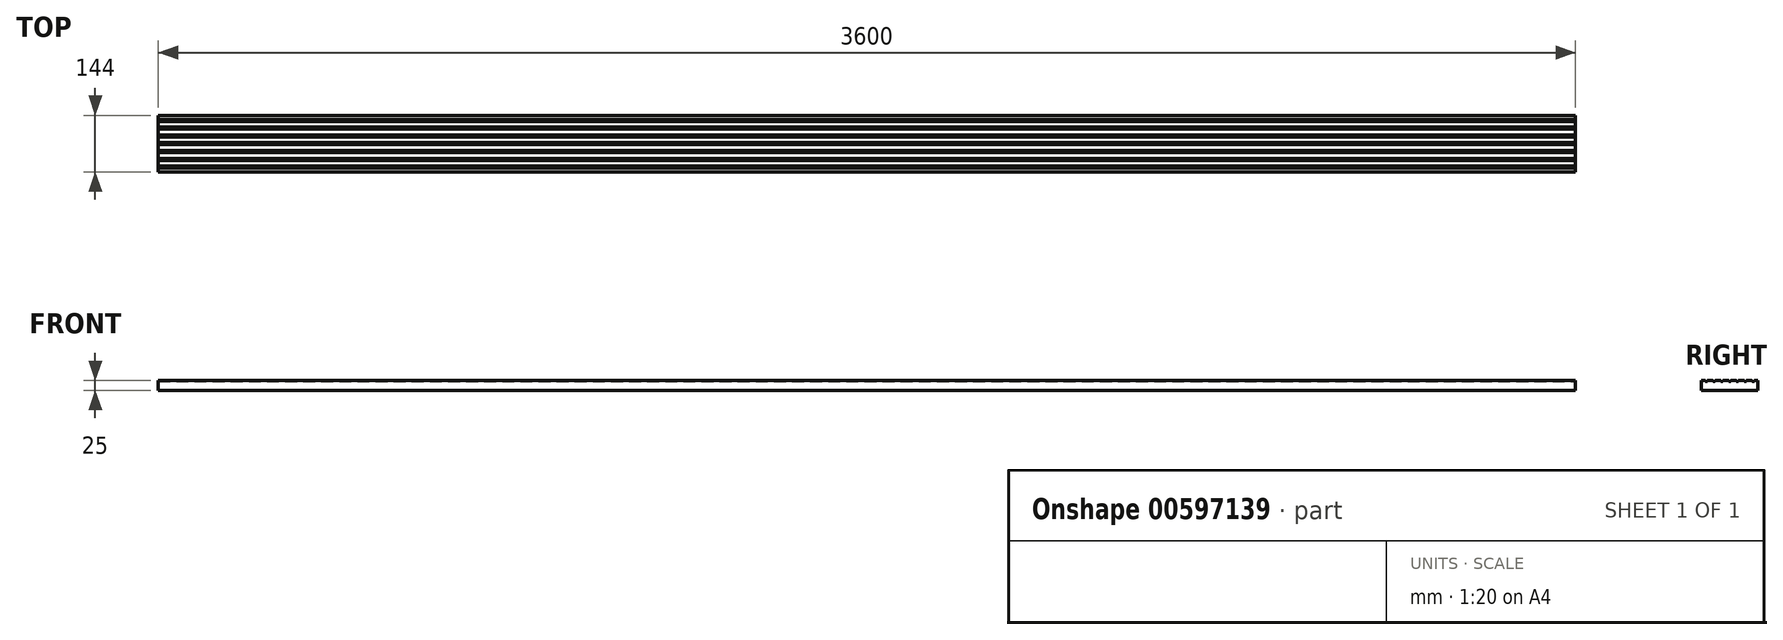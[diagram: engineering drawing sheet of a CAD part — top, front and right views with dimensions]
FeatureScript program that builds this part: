
annotation { "Feature Type Name" : "Feature", "Feature Type Description" : "" }
export const myFeature = defineFeature(function(context is Context, id is Id, definition is map)
    precondition{}
    {
        {
            var Q0;
            Q0=qCreatedBy(makeId("Right.planeOp"),FACE);
            var sketch = newSketch(context, id + "F0", { "sketchPlane" : qUnion([Q0])});
            skLineSegment(sketch, "E0.bottom", {"start": v(72, 12.5) * mm, "end": v(-72, 12.5) * mm});
            skLineSegment(sketch, "E0.top", {"start": v(72, -12.5) * mm, "end": v(-72, -12.5) * mm});
            skLineSegment(sketch, "E0.left", {"start": v(72, 12.5) * mm, "end": v(72, -12.5) * mm});
            skLineSegment(sketch, "E0.right", {"start": v(-72, 12.5) * mm, "end": v(-72, -12.5) * mm});
            skPoint(sketch, "E0.middle", {"position": v(0, 0) * mm});
            skSolve(sketch);
        }
        {
            var Q0;
            Q0 = qSketchRegion(id + "F0", true);
            extrude(context, id + "F1", {"entities" : qUnion([Q0]), "depth" : 3600 * mm, "offsetDistance" : 25 * mm});
        }
        {
            var Q0;
            Q0=makeQuery(id+"F1.opExtrude","CAP_FACE",FACE,{"disambiguationData":[OSD([sQuery(id+"F0.wireOp",EDGE,"E0.bottom"),sQuery(id+"F0.wireOp",EDGE,"E0.top"),sQuery(id+"F0.wireOp",EDGE,"E0.left"),sQuery(id+"F0.wireOp",EDGE,"E0.right")])],"isStart":false});
            var sketch = newSketch(context, id + "F2", { "sketchPlane" : qUnion([Q0])});
            skLineSegment(sketch, "E1", {"start": v(-72, 12.5) * mm, "end": v(-62, 12.5) * mm, "construction": true});
            skLineSegment(sketch, "E2", {"start": v(-62, 12.5) * mm, "end": v(-62, 10.5) * mm});
            skLineSegment(sketch, "E3", {"start": v(-62, 10.5) * mm, "end": v(-57, 10.5) * mm});
            skLineSegment(sketch, "E4", {"start": v(-57, 10.5) * mm, "end": v(-57, 12.5) * mm});
            skLineSegment(sketch, "E5", {"start": v(-62, 12.5) * mm, "end": v(-57, 12.5) * mm});
            skLineSegment(sketch, "E6", {"start": v(-57, 12.5) * mm, "end": v(-42.17, 12.5) * mm, "construction": true});
            skLineSegment(sketch, "E7", {"start": v(-42.17, 12.5) * mm, "end": v(-37.17, 12.5) * mm});
            skLineSegment(sketch, "E8", {"start": v(-37.17, 12.5) * mm, "end": v(-22.33, 12.5) * mm, "construction": true});
            skLineSegment(sketch, "E9", {"start": v(-22.33, 12.5) * mm, "end": v(-17.33, 12.5) * mm});
            skLineSegment(sketch, "E10", {"start": v(-17.33, 12.5) * mm, "end": v(-2.5, 12.5) * mm, "construction": true});
            skLineSegment(sketch, "E11", {"start": v(-2.5, 12.5) * mm, "end": v(2.5, 12.5) * mm});
            skLineSegment(sketch, "E12", {"start": v(2.5, 12.5) * mm, "end": v(17.33, 12.5) * mm, "construction": true});
            skLineSegment(sketch, "E13", {"start": v(17.33, 12.5) * mm, "end": v(22.33, 12.5) * mm});
            skLineSegment(sketch, "E14", {"start": v(22.33, 12.5) * mm, "end": v(37.17, 12.5) * mm, "construction": true});
            skLineSegment(sketch, "E15", {"start": v(37.17, 12.5) * mm, "end": v(42.17, 12.5) * mm});
            skLineSegment(sketch, "E16", {"start": v(42.17, 12.5) * mm, "end": v(57, 12.5) * mm, "construction": true});
            skLineSegment(sketch, "E17", {"start": v(57, 12.5) * mm, "end": v(62, 12.5) * mm});
            skLineSegment(sketch, "E18", {"start": v(62, 12.5) * mm, "end": v(72, 12.5) * mm, "construction": true});
            skLineSegment(sketch, "E19", {"start": v(-57, 10.5) * mm, "end": v(72, 10.5) * mm, "construction": true});
            skLineSegment(sketch, "E20", {"start": v(-42.17, 12.5) * mm, "end": v(-42.17, 10.5) * mm});
            skLineSegment(sketch, "E21", {"start": v(-42.17, 10.5) * mm, "end": v(-37.17, 10.5) * mm});
            skLineSegment(sketch, "E22", {"start": v(-37.17, 10.5) * mm, "end": v(-37.17, 12.5) * mm});
            skLineSegment(sketch, "E23", {"start": v(-22.33, 12.5) * mm, "end": v(-22.33, 10.5) * mm});
            skLineSegment(sketch, "E24", {"start": v(-22.33, 10.5) * mm, "end": v(-17.33, 10.5) * mm});
            skLineSegment(sketch, "E25", {"start": v(-17.33, 10.5) * mm, "end": v(-17.33, 12.5) * mm});
            skLineSegment(sketch, "E26", {"start": v(-2.5, 12.5) * mm, "end": v(-2.5, 10.5) * mm});
            skLineSegment(sketch, "E27", {"start": v(-2.5, 10.5) * mm, "end": v(2.5, 10.5) * mm});
            skLineSegment(sketch, "E28", {"start": v(2.5, 10.5) * mm, "end": v(2.5, 12.5) * mm});
            skLineSegment(sketch, "E29", {"start": v(17.33, 12.5) * mm, "end": v(17.33, 10.5) * mm});
            skLineSegment(sketch, "E30", {"start": v(17.33, 10.5) * mm, "end": v(22.33, 10.5) * mm});
            skLineSegment(sketch, "E31", {"start": v(22.33, 10.5) * mm, "end": v(22.33, 12.5) * mm});
            skLineSegment(sketch, "E32", {"start": v(37.17, 12.5) * mm, "end": v(37.17, 10.5) * mm});
            skLineSegment(sketch, "E33", {"start": v(37.17, 10.5) * mm, "end": v(42.17, 10.5) * mm});
            skLineSegment(sketch, "E34", {"start": v(42.17, 10.5) * mm, "end": v(42.17, 12.5) * mm});
            skLineSegment(sketch, "E35", {"start": v(57, 12.5) * mm, "end": v(57, 10.5) * mm});
            skLineSegment(sketch, "E36", {"start": v(57, 10.5) * mm, "end": v(62, 10.5) * mm});
            skLineSegment(sketch, "E37", {"start": v(62, 10.5) * mm, "end": v(62, 12.5) * mm});
            skSolve(sketch);
        }
        {
            var Q0;
            Q0 = qSketchRegion(id + "F2", true);
            extrude(context, id + "F3", {"entities" : qUnion([Q0]), "operationType" : NewBodyOperationType.REMOVE, "endBound" : BoundingType.THROUGH_ALL, "oppositeDirection" : true, "depth" : 25 * mm, "offsetDistance" : 25 * mm});
        }
        {
            var Q0;
            Q0=makeQuery(id+"F3.boolean.opBoolean","COPY",EDGE,{"derivedFrom":makeQuery(id+"F3.opExtrude","SWEPT_EDGE",EDGE,{"disambiguationData":[OSD([sQuery(id+"F0.wireOp",EDGE,"E0.bottom"),sQuery(id+"F2.wireOp",EDGE,"E2"),sQuery(id+"F2.wireOp",EDGE,"E5")])]})});
            var Q1;
            Q1=makeQuery(id+"F3.boolean.opBoolean","COPY",EDGE,{"derivedFrom":makeQuery(id+"F3.opExtrude","SWEPT_EDGE",EDGE,{"disambiguationData":[OSD([sQuery(id+"F2.wireOp",EDGE,"E2"),sQuery(id+"F2.wireOp",EDGE,"E3")])]})});
            var Q2;
            Q2=makeQuery(id+"F3.boolean.opBoolean","COPY",EDGE,{"derivedFrom":makeQuery(id+"F3.opExtrude","SWEPT_EDGE",EDGE,{"disambiguationData":[OSD([sQuery(id+"F0.wireOp",EDGE,"E0.bottom"),sQuery(id+"F2.wireOp",EDGE,"E4"),sQuery(id+"F2.wireOp",EDGE,"E5")])]})});
            var Q3;
            Q3=makeQuery(id+"F3.boolean.opBoolean","COPY",EDGE,{"derivedFrom":makeQuery(id+"F3.opExtrude","SWEPT_EDGE",EDGE,{"disambiguationData":[OSD([sQuery(id+"F2.wireOp",EDGE,"E3"),sQuery(id+"F2.wireOp",EDGE,"E4")])]})});
            var Q4;
            Q4=makeQuery(id+"F3.boolean.opBoolean","COPY",EDGE,{"derivedFrom":makeQuery(id+"F3.opExtrude","SWEPT_EDGE",EDGE,{"disambiguationData":[OSD([sQuery(id+"F0.wireOp",EDGE,"E0.bottom"),sQuery(id+"F2.wireOp",EDGE,"E7"),sQuery(id+"F2.wireOp",EDGE,"E22")])]})});
            var Q5;
            Q5=makeQuery(id+"F3.boolean.opBoolean","COPY",EDGE,{"derivedFrom":makeQuery(id+"F3.opExtrude","SWEPT_EDGE",EDGE,{"disambiguationData":[OSD([sQuery(id+"F2.wireOp",EDGE,"E21"),sQuery(id+"F2.wireOp",EDGE,"E22")])]})});
            var Q6;
            Q6=makeQuery(id+"F3.boolean.opBoolean","COPY",EDGE,{"derivedFrom":makeQuery(id+"F3.opExtrude","SWEPT_EDGE",EDGE,{"disambiguationData":[OSD([sQuery(id+"F0.wireOp",EDGE,"E0.bottom"),sQuery(id+"F2.wireOp",EDGE,"E9"),sQuery(id+"F2.wireOp",EDGE,"E25")])]})});
            var Q7;
            Q7=makeQuery(id+"F3.boolean.opBoolean","COPY",EDGE,{"derivedFrom":makeQuery(id+"F3.opExtrude","SWEPT_EDGE",EDGE,{"disambiguationData":[OSD([sQuery(id+"F2.wireOp",EDGE,"E24"),sQuery(id+"F2.wireOp",EDGE,"E25")])]})});
            var Q8;
            Q8=makeQuery(id+"F3.boolean.opBoolean","COPY",EDGE,{"derivedFrom":makeQuery(id+"F3.opExtrude","SWEPT_EDGE",EDGE,{"disambiguationData":[OSD([sQuery(id+"F0.wireOp",EDGE,"E0.bottom"),sQuery(id+"F2.wireOp",EDGE,"E11"),sQuery(id+"F2.wireOp",EDGE,"E28")])]})});
            var Q9;
            Q9=makeQuery(id+"F3.boolean.opBoolean","COPY",EDGE,{"derivedFrom":makeQuery(id+"F3.opExtrude","SWEPT_EDGE",EDGE,{"disambiguationData":[OSD([sQuery(id+"F2.wireOp",EDGE,"E27"),sQuery(id+"F2.wireOp",EDGE,"E28")])]})});
            var Q10;
            Q10=makeQuery(id+"F3.boolean.opBoolean","COPY",EDGE,{"derivedFrom":makeQuery(id+"F3.opExtrude","SWEPT_EDGE",EDGE,{"disambiguationData":[OSD([sQuery(id+"F0.wireOp",EDGE,"E0.bottom"),sQuery(id+"F2.wireOp",EDGE,"E13"),sQuery(id+"F2.wireOp",EDGE,"E31")])]})});
            var Q11;
            Q11=makeQuery(id+"F3.boolean.opBoolean","COPY",EDGE,{"derivedFrom":makeQuery(id+"F3.opExtrude","SWEPT_EDGE",EDGE,{"disambiguationData":[OSD([sQuery(id+"F2.wireOp",EDGE,"E30"),sQuery(id+"F2.wireOp",EDGE,"E31")])]})});
            var Q12;
            Q12=makeQuery(id+"F3.boolean.opBoolean","COPY",EDGE,{"derivedFrom":makeQuery(id+"F3.opExtrude","SWEPT_EDGE",EDGE,{"disambiguationData":[OSD([sQuery(id+"F0.wireOp",EDGE,"E0.bottom"),sQuery(id+"F2.wireOp",EDGE,"E15"),sQuery(id+"F2.wireOp",EDGE,"E34")])]})});
            var Q13;
            Q13=makeQuery(id+"F3.boolean.opBoolean","COPY",EDGE,{"derivedFrom":makeQuery(id+"F3.opExtrude","SWEPT_EDGE",EDGE,{"disambiguationData":[OSD([sQuery(id+"F2.wireOp",EDGE,"E33"),sQuery(id+"F2.wireOp",EDGE,"E34")])]})});
            var Q14;
            Q14=makeQuery(id+"F3.boolean.opBoolean","COPY",EDGE,{"derivedFrom":makeQuery(id+"F3.opExtrude","SWEPT_EDGE",EDGE,{"disambiguationData":[OSD([sQuery(id+"F0.wireOp",EDGE,"E0.bottom"),sQuery(id+"F2.wireOp",EDGE,"E17"),sQuery(id+"F2.wireOp",EDGE,"E37")])]})});
            var Q15;
            Q15=makeQuery(id+"F3.boolean.opBoolean","COPY",EDGE,{"derivedFrom":makeQuery(id+"F3.opExtrude","SWEPT_EDGE",EDGE,{"disambiguationData":[OSD([sQuery(id+"F2.wireOp",EDGE,"E36"),sQuery(id+"F2.wireOp",EDGE,"E37")])]})});
            var Q16;
            Q16=makeQuery(id+"F3.boolean.opBoolean","COPY",EDGE,{"derivedFrom":makeQuery(id+"F3.opExtrude","SWEPT_EDGE",EDGE,{"disambiguationData":[OSD([sQuery(id+"F0.wireOp",EDGE,"E0.bottom"),sQuery(id+"F2.wireOp",EDGE,"E17"),sQuery(id+"F2.wireOp",EDGE,"E35")])]})});
            var Q17;
            Q17=makeQuery(id+"F3.boolean.opBoolean","COPY",EDGE,{"derivedFrom":makeQuery(id+"F3.opExtrude","SWEPT_EDGE",EDGE,{"disambiguationData":[OSD([sQuery(id+"F2.wireOp",EDGE,"E35"),sQuery(id+"F2.wireOp",EDGE,"E36")])]})});
            var Q18;
            Q18=makeQuery(id+"F3.boolean.opBoolean","COPY",EDGE,{"derivedFrom":makeQuery(id+"F3.opExtrude","SWEPT_EDGE",EDGE,{"disambiguationData":[OSD([sQuery(id+"F0.wireOp",EDGE,"E0.bottom"),sQuery(id+"F2.wireOp",EDGE,"E15"),sQuery(id+"F2.wireOp",EDGE,"E32")])]})});
            var Q19;
            Q19=makeQuery(id+"F3.boolean.opBoolean","COPY",EDGE,{"derivedFrom":makeQuery(id+"F3.opExtrude","SWEPT_EDGE",EDGE,{"disambiguationData":[OSD([sQuery(id+"F2.wireOp",EDGE,"E32"),sQuery(id+"F2.wireOp",EDGE,"E33")])]})});
            var Q20;
            Q20=makeQuery(id+"F3.boolean.opBoolean","COPY",EDGE,{"derivedFrom":makeQuery(id+"F3.opExtrude","SWEPT_EDGE",EDGE,{"disambiguationData":[OSD([sQuery(id+"F0.wireOp",EDGE,"E0.bottom"),sQuery(id+"F2.wireOp",EDGE,"E13"),sQuery(id+"F2.wireOp",EDGE,"E29")])]})});
            var Q21;
            Q21=makeQuery(id+"F3.boolean.opBoolean","COPY",EDGE,{"derivedFrom":makeQuery(id+"F3.opExtrude","SWEPT_EDGE",EDGE,{"disambiguationData":[OSD([sQuery(id+"F2.wireOp",EDGE,"E29"),sQuery(id+"F2.wireOp",EDGE,"E30")])]})});
            var Q22;
            Q22=makeQuery(id+"F3.boolean.opBoolean","COPY",EDGE,{"derivedFrom":makeQuery(id+"F3.opExtrude","SWEPT_EDGE",EDGE,{"disambiguationData":[OSD([sQuery(id+"F0.wireOp",EDGE,"E0.bottom"),sQuery(id+"F2.wireOp",EDGE,"E11"),sQuery(id+"F2.wireOp",EDGE,"E26")])]})});
            var Q23;
            Q23=makeQuery(id+"F3.boolean.opBoolean","COPY",EDGE,{"derivedFrom":makeQuery(id+"F3.opExtrude","SWEPT_EDGE",EDGE,{"disambiguationData":[OSD([sQuery(id+"F2.wireOp",EDGE,"E26"),sQuery(id+"F2.wireOp",EDGE,"E27")])]})});
            var Q24;
            Q24=makeQuery(id+"F3.boolean.opBoolean","COPY",EDGE,{"derivedFrom":makeQuery(id+"F3.opExtrude","SWEPT_EDGE",EDGE,{"disambiguationData":[OSD([sQuery(id+"F0.wireOp",EDGE,"E0.bottom"),sQuery(id+"F2.wireOp",EDGE,"E9"),sQuery(id+"F2.wireOp",EDGE,"E23")])]})});
            var Q25;
            Q25=makeQuery(id+"F3.boolean.opBoolean","COPY",EDGE,{"derivedFrom":makeQuery(id+"F3.opExtrude","SWEPT_EDGE",EDGE,{"disambiguationData":[OSD([sQuery(id+"F2.wireOp",EDGE,"E23"),sQuery(id+"F2.wireOp",EDGE,"E24")])]})});
            var Q26;
            Q26=makeQuery(id+"F3.boolean.opBoolean","COPY",EDGE,{"derivedFrom":makeQuery(id+"F3.opExtrude","SWEPT_EDGE",EDGE,{"disambiguationData":[OSD([sQuery(id+"F0.wireOp",EDGE,"E0.bottom"),sQuery(id+"F2.wireOp",EDGE,"E7"),sQuery(id+"F2.wireOp",EDGE,"E20")])]})});
            var Q27;
            Q27=makeQuery(id+"F3.boolean.opBoolean","COPY",EDGE,{"derivedFrom":makeQuery(id+"F3.opExtrude","SWEPT_EDGE",EDGE,{"disambiguationData":[OSD([sQuery(id+"F2.wireOp",EDGE,"E20"),sQuery(id+"F2.wireOp",EDGE,"E21")])]})});
            fillet(context, id + "F4", {"entities" : qUnion([Q0, Q1, Q2, Q3, Q4, Q5, Q6, Q7, Q8, Q9, Q10, Q11, Q12, Q13, Q14, Q15, Q16, Q17, Q18, Q19, Q20, Q21, Q22, Q23, Q24, Q25, Q26, Q27]), "radius" : 0.5 * mm, "tangentPropagation" : true, "allowEdgeOverflow" : false});
        }
    });
